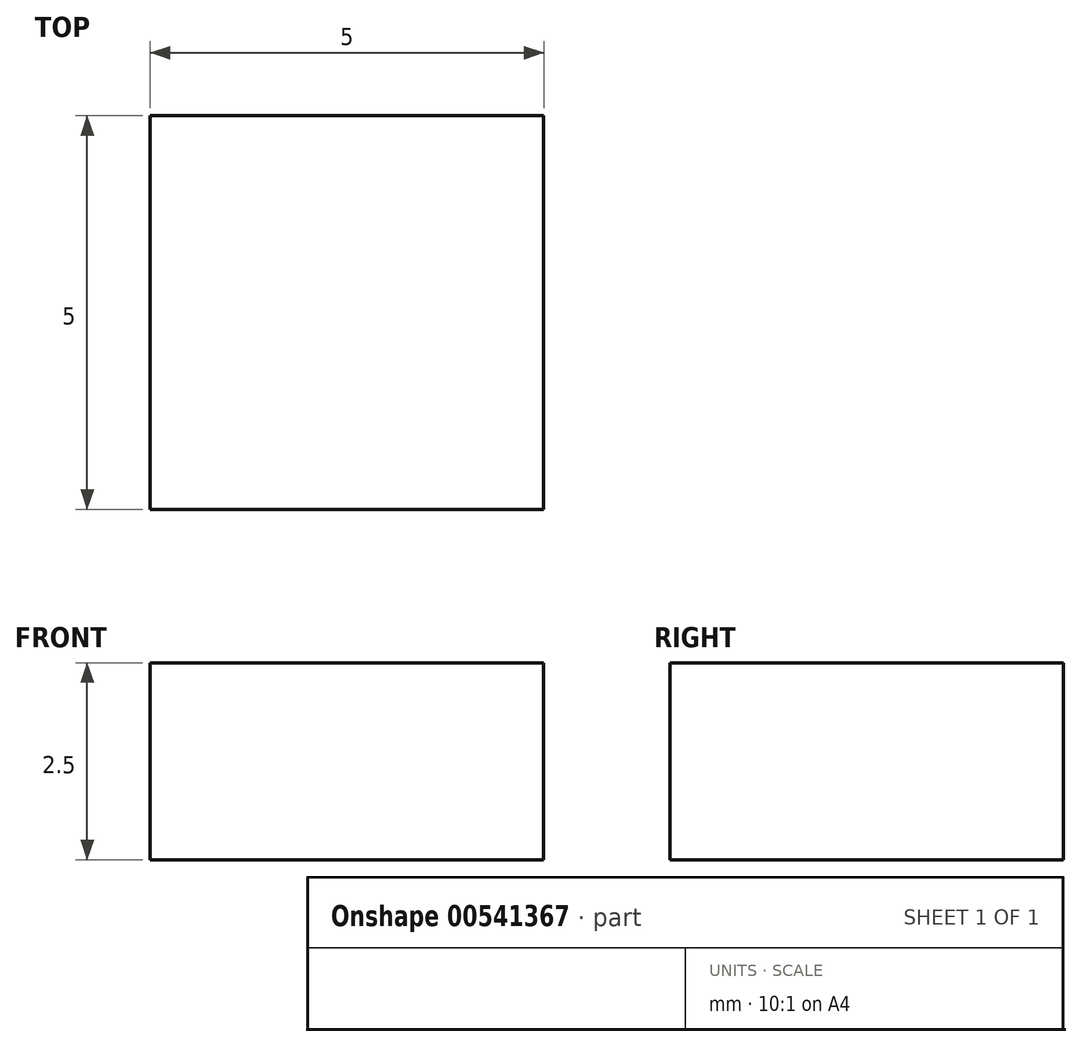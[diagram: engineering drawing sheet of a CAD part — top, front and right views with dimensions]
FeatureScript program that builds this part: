
annotation { "Feature Type Name" : "Feature", "Feature Type Description" : "" }
export const myFeature = defineFeature(function(context is Context, id is Id, definition is map)
    precondition{}
    {
        {
            var Q0;
            Q0=qCreatedBy(makeId("Top.planeOp"),FACE);
            var sketch = newSketch(context, id + "F0", { "sketchPlane" : qUnion([Q0])});
            skLineSegment(sketch, "E0.bottom", {"start": v(-9.51, 0) * mm, "end": v(-4.51, 0) * mm});
            skLineSegment(sketch, "E0.top", {"start": v(-9.51, 5) * mm, "end": v(-4.51, 5) * mm});
            skLineSegment(sketch, "E0.left", {"start": v(-9.51, 0) * mm, "end": v(-9.51, 5) * mm});
            skLineSegment(sketch, "E0.right", {"start": v(-4.51, 0) * mm, "end": v(-4.51, 5) * mm});
            skSolve(sketch);
        }
        {
            var Q0;
            Q0=makeQuery(id+"F0.imprint","IMPRINT",FACE,{"disambiguationData":[TD([[makeQuery(id+"F0.imprint","IMPRINT",EDGE,{"derivedFrom":sQuery(id+"F0.wireOp",EDGE,"E0.bottom")}),1.0]])]});
            extrude(context, id + "F1", {"entities" : qUnion([Q0]), "depth" : 2.5 * mm, "offsetDistance" : 25 * mm});
        }
    });
